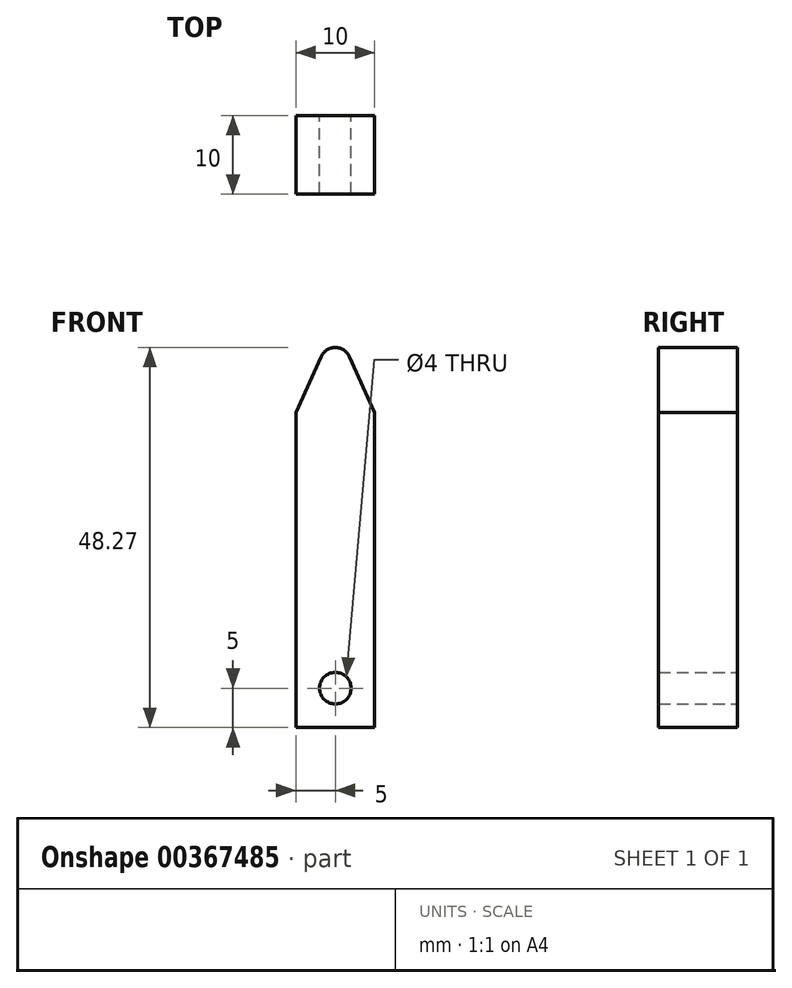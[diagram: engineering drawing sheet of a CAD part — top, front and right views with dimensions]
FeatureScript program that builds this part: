
annotation { "Feature Type Name" : "Feature", "Feature Type Description" : "" }
export const myFeature = defineFeature(function(context is Context, id is Id, definition is map)
    precondition{}
    {
        {
            var Q0;
            Q0=qCreatedBy(makeId("Front.planeOp"),FACE);
            var sketch = newSketch(context, id + "F0", { "sketchPlane" : qUnion([Q0])});
            skLineSegment(sketch, "E0.top", {"start": v(5, -20) * mm, "end": v(-5, -20) * mm});
            skLineSegment(sketch, "E0.left", {"start": v(5, 20) * mm, "end": v(5, -20) * mm});
            skLineSegment(sketch, "E0.right", {"start": v(-5, 20) * mm, "end": v(-5, -20) * mm});
            skPoint(sketch, "E0.middle", {"position": v(0, 0) * mm});
            skArc(sketch, "E1", {"start": v(1.83, 27.09) * mm, "mid": v(0, 28.27) * mm, "end": v(-1.83, 27.09) * mm});
            skLineSegment(sketch, "E2", {"start": v(-5, 20) * mm, "end": v(-1.83, 27.09) * mm});
            skLineSegment(sketch, "E3", {"start": v(5, 20) * mm, "end": v(1.83, 27.09) * mm});
            skCircle(sketch, "E4", {"center": v(0, -15) * mm, "radius": 2 * mm});
            skSolve(sketch);
        }
        {
            var Q0;
            Q0=makeQuery(id+"F0.imprint","IMPRINT",FACE,{"disambiguationData":[TD([[makeQuery(id+"F0.imprint","IMPRINT",EDGE,{"derivedFrom":sQuery(id+"F0.wireOp",EDGE,"E0.top")}),-1.0]])]});
            extrude(context, id + "F1", {"entities" : qUnion([Q0]), "depth" : 10 * mm});
        }
    });
